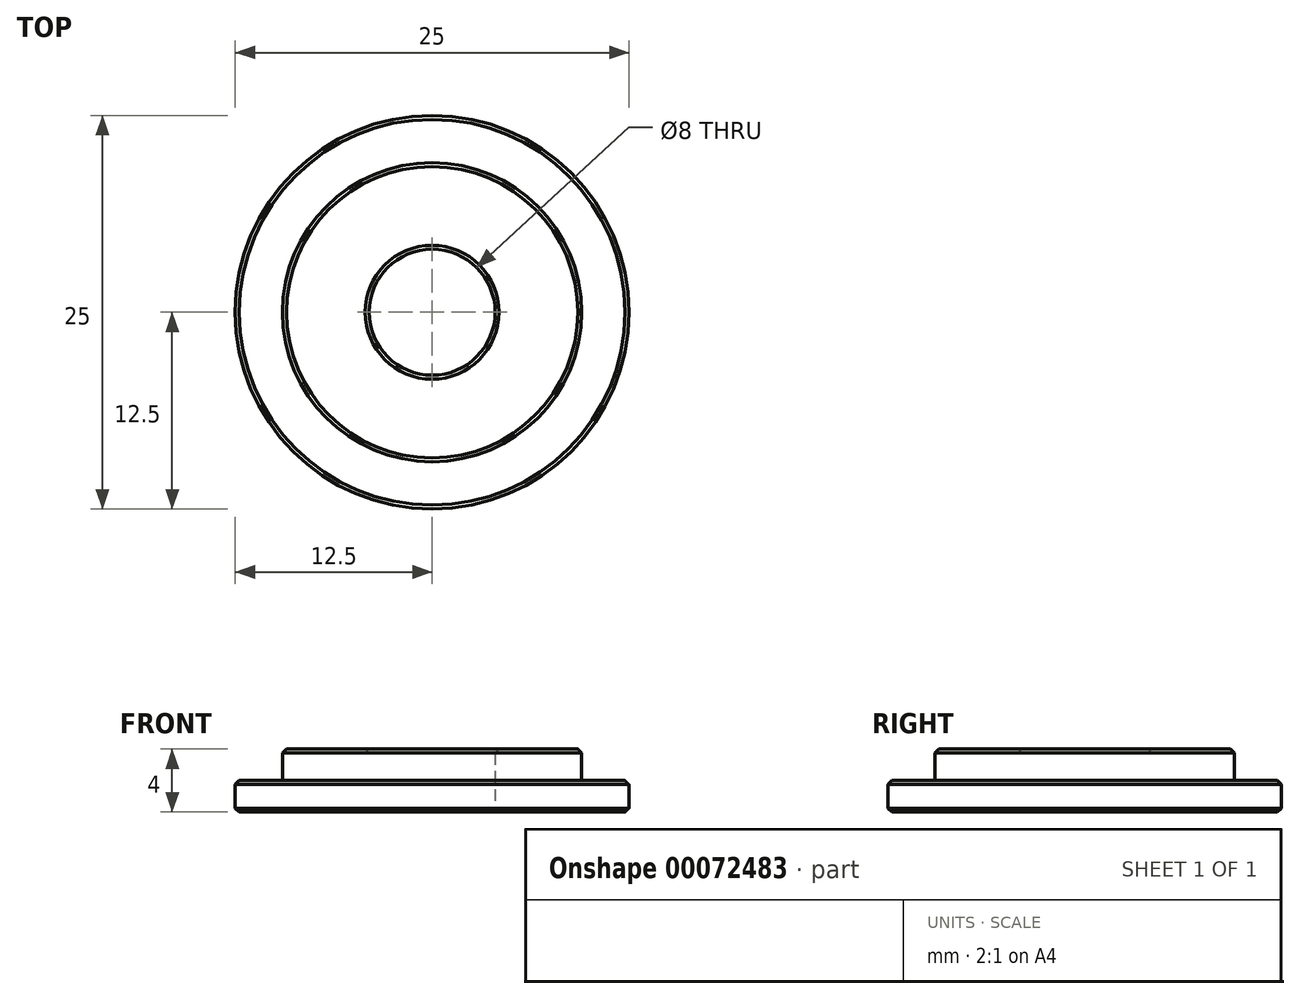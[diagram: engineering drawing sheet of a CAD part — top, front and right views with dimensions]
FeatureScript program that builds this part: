
annotation { "Feature Type Name" : "Feature", "Feature Type Description" : "" }
export const myFeature = defineFeature(function(context is Context, id is Id, definition is map)
    precondition{}
    {
        {
            var Q0;
            Q0=qCreatedBy(makeId("Top.planeOp"),FACE);
            var sketch = newSketch(context, id + "F0", { "sketchPlane" : qUnion([Q0])});
            skCircle(sketch, "E0", {"center": v(0, 0) * mm, "radius": 4 * mm});
            skCircle(sketch, "E1", {"center": v(0, 0) * mm, "radius": 12.5 * mm});
            skSolve(sketch);
        }
        {
            var Q0;
            Q0=makeQuery(id+"F0.imprint","IMPRINT",FACE,{"disambiguationData":[TD([[makeQuery(id+"F0.imprint","IMPRINT",EDGE,{"derivedFrom":sQuery(id+"F0.wireOp",EDGE,"E0")}),-1.0]])]});
            extrude(context, id + "F1", {"entities" : qUnion([Q0]), "depth" : 2 * mm});
        }
        {
            var Q0;
            Q0=makeQuery(id+"F1.opExtrude","CAP_FACE",FACE,{"disambiguationData":[OSD([sQuery(id+"F0.wireOp",EDGE,"E0"),sQuery(id+"F0.wireOp",EDGE,"E1")])],"isStart":false});
            var sketch = newSketch(context, id + "F2", { "sketchPlane" : qUnion([Q0])});
            skCircle(sketch, "E2", {"center": v(0, 0) * mm, "radius": 9.5 * mm});
            skSolve(sketch);
        }
        {
            var Q0;
            Q0=makeQuery(id+"F2.imprint","IMPRINT",FACE,{"disambiguationData":[TD([[makeQuery(id+"F2.imprint","IMPRINT",EDGE,{"derivedFrom":sQuery(id+"F2.wireOp",EDGE,"E2")}),1.0]])]});
            extrude(context, id + "F3", {"entities" : qUnion([Q0]), "operationType" : NewBodyOperationType.ADD, "depth" : 2 * mm});
        }
        {
            var Q0;
            Q0=makeQuery(id+"F3.opExtrude","CAP_FACE",FACE,{"disambiguationData":[OSD([sQuery(id+"F0.wireOp",EDGE,"E0"),sQuery(id+"F2.wireOp",EDGE,"E2")])],"isStart":false});
            var Q1;
            Q1=makeQuery(id+"F1.opExtrude","CAP_EDGE",EDGE,{"disambiguationData":[OSD([sQuery(id+"F0.wireOp",EDGE,"E1")])],"isStart":false});
            var Q2;
            Q2=makeQuery(id+"F1.opExtrude","CAP_FACE",FACE,{"disambiguationData":[OSD([sQuery(id+"F0.wireOp",EDGE,"E0"),sQuery(id+"F0.wireOp",EDGE,"E1")])],"isStart":true});
            chamfer(context, id + "F4", {"entities" : qUnion([Q0, Q1, Q2]), "width" : .25 * mm, "tangentPropagation" : true});
        }
    });
